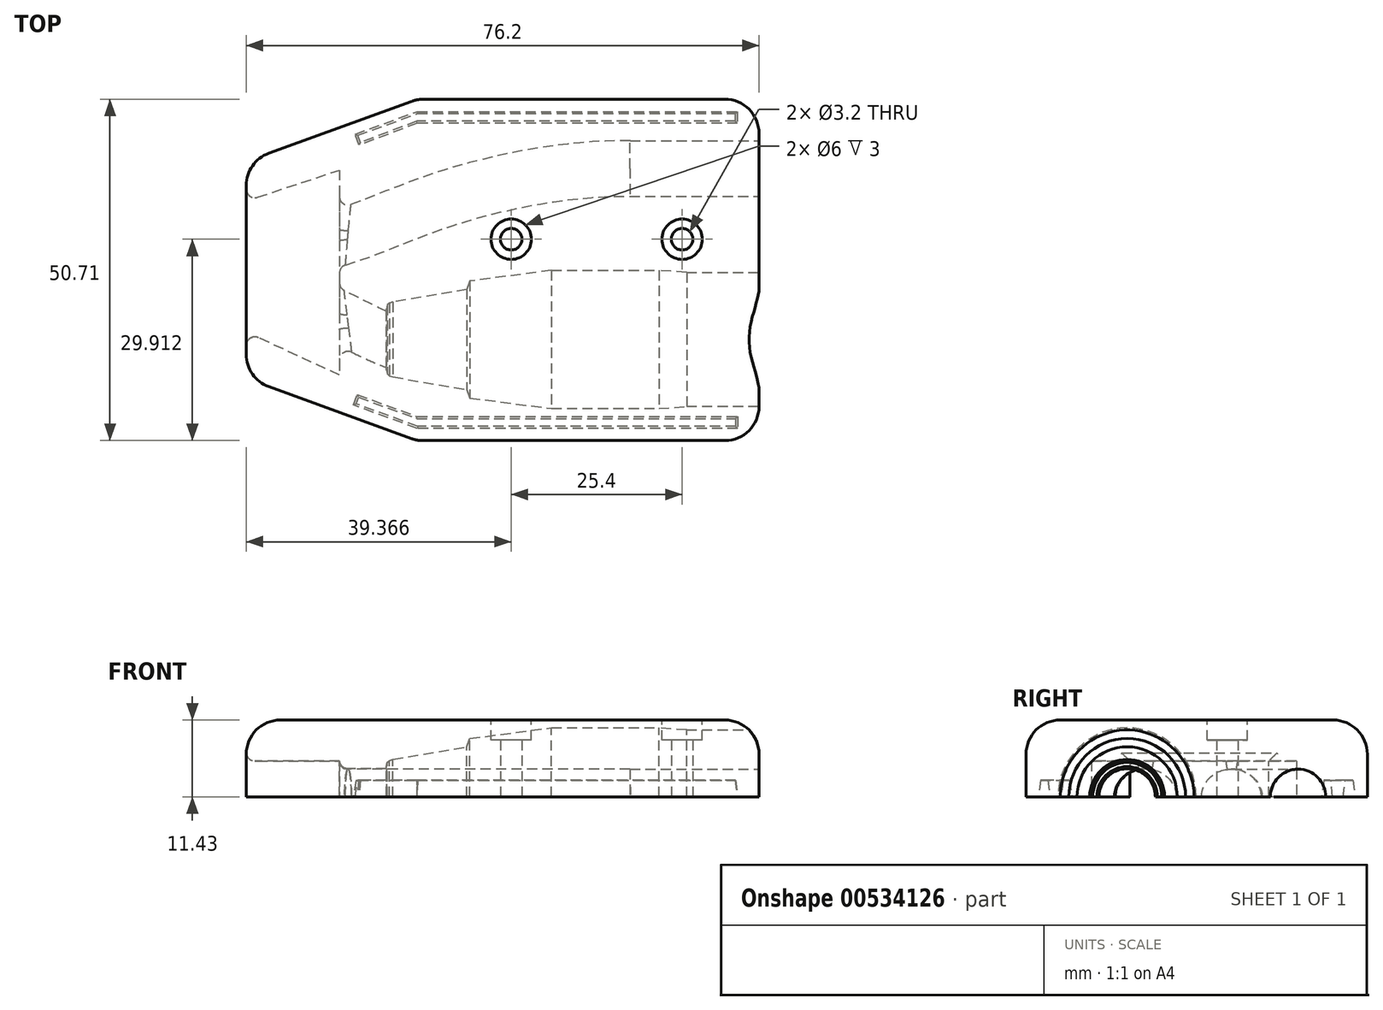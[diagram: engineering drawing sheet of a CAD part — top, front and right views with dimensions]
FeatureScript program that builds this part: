
annotation { "Feature Type Name" : "Feature", "Feature Type Description" : "" }
export const myFeature = defineFeature(function(context is Context, id is Id, definition is map)
    precondition{}
    {
        {
            var Q0;
            Q0=qCreatedBy(makeId("Top.planeOp"),FACE);
            var sketch = newSketch(context, id + "F0", { "sketchPlane" : qUnion([Q0])});
            skLineSegment(sketch, "E0", {"start": v(-28.61, 2.44) * mm, "end": v(45.8, 2.44) * mm});
            skLineSegment(sketch, "E1", {"start": v(45.8, 2.44) * mm, "end": v(45.8, -7.5) * mm});
            skLineSegment(sketch, "E2", {"start": v(45.8, -7.5) * mm, "end": v(33.92, -7.5) * mm});
            skLineSegment(sketch, "E3", {"start": v(33.92, -7.5) * mm, "end": v(31.07, -7.5) * mm});
            skLineSegment(sketch, "E4", {"start": v(31.07, -7.5) * mm, "end": v(15.98, -7.5) * mm});
            skLineSegment(sketch, "E5", {"start": v(15.98, -7.5) * mm, "end": v(11.85, -7.82) * mm});
            skLineSegment(sketch, "E6", {"start": v(11.85, -7.82) * mm, "end": v(-4.1, -7.82) * mm});
            skLineSegment(sketch, "E7", {"start": v(-4.1, -7.82) * mm, "end": v(-16.21, -6.24) * mm});
            skLineSegment(sketch, "E8", {"start": v(-16.21, -6.24) * mm, "end": v(-16.67, -5) * mm});
            skLineSegment(sketch, "E9", {"start": v(-16.67, -5) * mm, "end": v(-27.65, -3.12) * mm});
            skLineSegment(sketch, "E10", {"start": v(-27.65, -3.12) * mm, "end": v(-28.19, -2.96) * mm});
            skLineSegment(sketch, "E11", {"start": v(-28.19, -2.96) * mm, "end": v(-28.49, -2.68) * mm});
            skLineSegment(sketch, "E12", {"start": v(-28.49, -2.68) * mm, "end": v(-28.63, -2.06) * mm});
            skLineSegment(sketch, "E13", {"start": v(-28.63, -2.06) * mm, "end": v(-28.61, 2.44) * mm});
            skLineSegment(sketch, "E14.top", {"start": v(32.8, 22.64) * mm, "end": v(45.8, 22.64) * mm});
            skLineSegment(sketch, "E14.right", {"start": v(45.8, 27.84) * mm, "end": v(45.8, 22.64) * mm});
            skLineSegment(sketch, "E15", {"start": v(32.8, 23.72) * mm, "end": v(24.8, 23.72) * mm});
            skLineSegment(sketch, "E16", {"start": v(24.8, 23.72) * mm, "end": v(24.8, 27.84) * mm});
            skLineSegment(sketch, "E17", {"start": v(45.8, 27.84) * mm, "end": v(24.8, 27.84) * mm});
            skLineSegment(sketch, "E18", {"start": v(32.8, 22.64) * mm, "end": v(32.8, 23.72) * mm});
            skLineSegment(sketch, "E19.MirrorCS", {"start": v(32.8, 33.05) * mm, "end": v(32.8, 31.97) * mm});
            skLineSegment(sketch, "E20.MirrorCS", {"start": v(32.8, 33.05) * mm, "end": v(45.8, 33.05) * mm});
            skLineSegment(sketch, "E21.MirrorCS", {"start": v(45.8, 27.84) * mm, "end": v(45.8, 33.05) * mm});
            skLineSegment(sketch, "E22.MirrorCS", {"start": v(24.8, 31.97) * mm, "end": v(24.8, 27.84) * mm});
            skLineSegment(sketch, "E23.MirrorCS", {"start": v(32.8, 31.97) * mm, "end": v(24.8, 31.97) * mm});
            skLineSegment(sketch, "E24.MirrorCS", {"start": v(-28.19, 7.85) * mm, "end": v(-28.49, 7.56) * mm});
            skLineSegment(sketch, "E25.MirrorCS", {"start": v(-28.49, 7.56) * mm, "end": v(-28.63, 6.94) * mm});
            skLineSegment(sketch, "E26.MirrorCS", {"start": v(33.92, 12.39) * mm, "end": v(31.07, 12.39) * mm});
            skLineSegment(sketch, "E27.MirrorCS", {"start": v(-27.65, 8) * mm, "end": v(-28.19, 7.85) * mm});
            skLineSegment(sketch, "E28.MirrorCS", {"start": v(-16.21, 11.12) * mm, "end": v(-16.67, 9.89) * mm});
            skLineSegment(sketch, "E29.MirrorCS", {"start": v(-16.67, 9.89) * mm, "end": v(-27.65, 8) * mm});
            skLineSegment(sketch, "E30.MirrorCS", {"start": v(11.85, 12.7) * mm, "end": v(-4.1, 12.7) * mm});
            skLineSegment(sketch, "E31.MirrorCS", {"start": v(45.8, 12.39) * mm, "end": v(33.92, 12.39) * mm});
            skLineSegment(sketch, "E32.MirrorCS", {"start": v(-4.1, 12.7) * mm, "end": v(-16.21, 11.12) * mm});
            skLineSegment(sketch, "E33.MirrorCS", {"start": v(15.98, 12.39) * mm, "end": v(11.85, 12.7) * mm});
            skLineSegment(sketch, "E34.MirrorCS", {"start": v(31.07, 12.39) * mm, "end": v(15.98, 12.39) * mm});
            skLineSegment(sketch, "E35.MirrorCS", {"start": v(45.8, 2.44) * mm, "end": v(45.8, 12.39) * mm});
            skLineSegment(sketch, "E36.MirrorCS", {"start": v(-28.63, 6.94) * mm, "end": v(-28.61, 2.44) * mm});
            skSolve(sketch);
        }
        {
            var Q0;
            Q0=qCreatedBy(makeId("Top.planeOp"),FACE);
            var sketch = newSketch(context, id + "F1", { "sketchPlane" : qUnion([Q0])});
            skLineSegment(sketch, "E37.0", {"start": v(45.8, 2.44) * mm, "end": v(45.8, -7.5) * mm});
            skLineSegment(sketch, "E38.0", {"start": v(45.8, 27.84) * mm, "end": v(45.8, 22.64) * mm});
            skLineSegment(sketch, "E39", {"start": v(26.75, 38.13) * mm, "end": v(26.75, -12.58) * mm});
            skLineSegment(sketch, "E40", {"start": v(26.75, -12.58) * mm, "end": v(-24.05, -12.58) * mm});
            skLineSegment(sketch, "E41", {"start": v(-24.05, -12.58) * mm, "end": v(-49.45, -3.34) * mm});
            skLineSegment(sketch, "E42", {"start": v(-49.45, -3.34) * mm, "end": v(-49.45, 28.88) * mm});
            skLineSegment(sketch, "E43", {"start": v(-49.45, 28.88) * mm, "end": v(-24.05, 38.13) * mm});
            skLineSegment(sketch, "E44", {"start": v(-24.05, 38.13) * mm, "end": v(26.75, 38.13) * mm});
            skLineSegment(sketch, "E45.0", {"start": v(45.8, 27.84) * mm, "end": v(45.8, 33.05) * mm});
            skSolve(sketch);
        }
        {
            var Q0;
            Q0=qSketchRegion(id+"F1",true);
            extrude(context, id + "F2", {"entities" : qUnion([Q0]), "oppositeDirection" : true, "depth" : 0 * mm, "offsetDistance" : 25.4 * mm, "hasSecondDirection" : true, "secondDirectionOppositeDirection" : false, "secondDirectionDepth" : 11.43 * mm});
        }
        {
            var Q0;
            Q0=makeQuery(id+"F0.imprint","IMPRINT",FACE,{"disambiguationData":[TD([[makeQuery(id+"F0.imprint","IMPRINT",EDGE,{"derivedFrom":sQuery(id+"F0.wireOp",EDGE,"E0")}),-1.0]])]});
            var Q1;
            Q1=sQuery(id+"F0.wireOp",EDGE,"E0");
            revolve(context, id + "F3", {"operationType" : NewBodyOperationType.REMOVE, "entities" : qUnion([Q0]), "axis" : qUnion([Q1]), "revolveType" : RevolveType.FULL, "oppositeDirection" : true});
        }
        {
            var Q0;
            Q0=makeQuery(id+"F0.imprint","IMPRINT",FACE,{"disambiguationData":[TD([[makeQuery(id+"F0.imprint","IMPRINT",EDGE,{"derivedFrom":sQuery(id+"F0.wireOp",EDGE,"E14.top")}),1.0]])]});
            var Q1;
            Q1=sQuery(id+"F0.wireOp",EDGE,"E17");
            revolve(context, id + "F4", {"operationType" : NewBodyOperationType.REMOVE, "entities" : qUnion([Q0]), "axis" : qUnion([Q1]), "revolveType" : RevolveType.FULL});
        }
        {
            var Q0;
            Q0=qCreatedBy(makeId("Top.planeOp"),FACE);
            var sketch = newSketch(context, id + "F5", { "sketchPlane" : qUnion([Q0])});
            skLineSegment(sketch, "E46.0", {"start": v(-28.61, 2.44) * mm, "end": v(45.8, 2.44) * mm});
            skFitSpline(sketch, "E47", {"points": [v(-28.61, 2.44) * mm, v(-48.07, 10.49) * mm, v(-83.77, 9.93) * mm], "startDerivative": vector(-48.46, 20.5) * mm, "endDerivative": vector(-77.25, 2.74) * mm});
            skSolve(sketch);
        }
        {
            var Q0;
            Q0=sQuery(id+"F5.wireOp",VERTEX,"E47.0.internal");
            var Q1;
            Q1=sQuery(id+"F5.wireOp",EDGE,"E46.0");
            cPlane(context, id + "F6", {"entities" : qUnion([Q0, Q1]), "cplaneType" : CPlaneType.LINE_POINT, "offset" : 25.4 * mm, "width" : 152.4 * mm, "height" : 152.4 * mm});
        }
        {
            var Q0;
            Q0=qCreatedBy(id+"F6.planeOp",FACE);
            var sketch = newSketch(context, id + "F7", { "sketchPlane" : qUnion([Q0])});
            skCircle(sketch, "E48", {"center": v(2.44, 0) * mm, "radius": 4.2 * mm});
            skSolve(sketch);
        }
        {
            var Q0;
            Q0=qSketchRegion(id+"F7",true);
            var Q1;
            Q1=sQuery(id+"F5.wireOp",EDGE,"E47");
            sweep(context, id + "F8", {"operationType" : NewBodyOperationType.REMOVE, "profiles" : qUnion([Q0]), "path" : qUnion([Q1])});
        }
        {
            var Q0;
            Q0=sQuery(id+"F0.wireOp",VERTEX,"E22.MirrorCS.end");
            var Q1;
            Q1=sQuery(id+"F0.wireOp",EDGE,"E17");
            cPlane(context, id + "F9", {"entities" : qUnion([Q0, Q1]), "cplaneType" : CPlaneType.LINE_POINT, "offset" : 25.4 * mm, "width" : 152.4 * mm, "height" : 152.4 * mm});
        }
        {
            var Q0;
            Q0=qCreatedBy(makeId("Top.planeOp"),FACE);
            var sketch = newSketch(context, id + "F10", { "sketchPlane" : qUnion([Q0])});
            skLineSegment(sketch, "E49", {"start": v(24.8, 27.84) * mm, "end": v(7.57, 27.84) * mm});
            skFitSpline(sketch, "E50", {"points": [v(7.57, 27.84) * mm, v(-20.4, 23.18) * mm, v(-39.19, 16.58) * mm, v(-88.02, 16.43) * mm], "startDerivative": vector(-85.25, 1.29) * mm, "endDerivative": vector(-186.21, 7.59) * mm});
            skSolve(sketch);
        }
        {
            var Q0;
            Q0=qCreatedBy(id+"F9.planeOp",FACE);
            var sketch = newSketch(context, id + "F11", { "sketchPlane" : qUnion([Q0])});
            skCircle(sketch, "E51", {"center": v(-27.84, 0) * mm, "radius": 4.12 * mm});
            skSolve(sketch);
        }
        {
            var Q0;
            Q0=qSketchRegion(id+"F11",true);
            var Q1;
            Q1=sQuery(id+"F10.wireOp",EDGE,"E49");
            var Q2;
            Q2=sQuery(id+"F10.wireOp",EDGE,"E50");
            sweep(context, id + "F12", {"operationType" : NewBodyOperationType.REMOVE, "profiles" : qUnion([Q0]), "path" : qUnion([Q1, Q2])});
        }
        {
            var Q0;
            Q0=qCreatedBy(makeId("Top.planeOp"),FACE);
            var sketch = newSketch(context, id + "F13", { "sketchPlane" : qUnion([Q0])});
            skLineSegment(sketch, "E52", {"start": v(-49.97, 22.84) * mm, "end": v(-35.6, 27.6) * mm});
            skLineSegment(sketch, "E53", {"start": v(-35.6, 27.6) * mm, "end": v(-35.6, -2.85) * mm});
            skLineSegment(sketch, "E54", {"start": v(-35.6, -2.85) * mm, "end": v(-49.98, 3.8) * mm});
            skLineSegment(sketch, "E55", {"start": v(-49.97, 22.84) * mm, "end": v(-49.98, 3.8) * mm});
            skSolve(sketch);
        }
        {
            var Q0;
            Q0=qCreatedBy(makeId("Top.planeOp"),FACE);
            var sketch = newSketch(context, id + "F14", { "sketchPlane" : qUnion([Q0])});
            skCircle(sketch, "E56", {"center": v(-10.08, 17.33) * mm, "radius": 1.6 * mm});
            skCircle(sketch, "E57", {"center": v(15.32, 17.33) * mm, "radius": 1.6 * mm});
            skLineSegment(sketch, "E58.0", {"start": v(-24.05, 38.13) * mm, "end": v(26.75, 38.13) * mm});
            skLineSegment(sketch, "E59.0", {"start": v(26.75, -12.58) * mm, "end": v(-24.05, -12.58) * mm});
            skLineSegment(sketch, "E60.0", {"start": v(-49.45, 28.88) * mm, "end": v(-24.05, 38.13) * mm});
            skLineSegment(sketch, "E61.0", {"start": v(-24.05, -12.58) * mm, "end": v(-49.45, -3.34) * mm});
            skSolve(sketch);
        }
        {
            var Q0;
            Q0=qCreatedBy(makeId("Top.planeOp"),FACE);
            var sketch = newSketch(context, id + "F15", { "sketchPlane" : qUnion([Q0])});
            skLineSegment(sketch, "E62.0", {"start": v(-49.45, 28.88) * mm, "end": v(-24.05, 38.13) * mm});
            skLineSegment(sketch, "E63.0", {"start": v(-24.05, 38.13) * mm, "end": v(26.75, 38.13) * mm});
            skLineSegment(sketch, "E64.0", {"start": v(-24.05, -12.58) * mm, "end": v(-49.45, -3.34) * mm});
            skLineSegment(sketch, "E65.1", {"start": v(26.75, -12.58) * mm, "end": v(-24.05, -12.58) * mm});
            skLineSegment(sketch, "E66", {"start": v(-33.28, 32.94) * mm, "end": v(-24.05, 36.3) * mm});
            skLineSegment(sketch, "E67", {"start": v(-24.05, 36.3) * mm, "end": v(23.52, 36.3) * mm});
            skLineSegment(sketch, "E68", {"start": v(23.52, 36.3) * mm, "end": v(23.52, 34.55) * mm});
            skLineSegment(sketch, "E69", {"start": v(23.52, 34.55) * mm, "end": v(-24.05, 34.55) * mm});
            skLineSegment(sketch, "E70", {"start": v(-33.28, 32.94) * mm, "end": v(-32.69, 31.3) * mm});
            skLineSegment(sketch, "E71", {"start": v(-32.69, 31.3) * mm, "end": v(-24.05, 34.55) * mm});
            skLineSegment(sketch, "E72", {"start": v(-33.53, -7.3) * mm, "end": v(-24.05, -10.76) * mm});
            skLineSegment(sketch, "E73", {"start": v(-24.05, -10.76) * mm, "end": v(23.57, -10.76) * mm});
            skLineSegment(sketch, "E74", {"start": v(23.57, -10.76) * mm, "end": v(23.57, -9) * mm});
            skLineSegment(sketch, "E75", {"start": v(23.57, -9) * mm, "end": v(-24.05, -9) * mm});
            skLineSegment(sketch, "E76", {"start": v(-24.05, -9) * mm, "end": v(-32.97, -5.76) * mm});
            skLineSegment(sketch, "E77", {"start": v(-32.97, -5.76) * mm, "end": v(-33.53, -7.3) * mm});
            skSolve(sketch);
        }
        {
            var Q0;
            Q0 = qSketchRegion(id + "F13", true);
            extrude(context, id + "F16", {"entities" : qUnion([Q0]), "operationType" : NewBodyOperationType.REMOVE, "depth" : 5.33 * mm, "offsetDistance" : 25.4 * mm});
        }
        {
            var Q0;
            Q0 = qSketchRegion(id + "F15", true);
            extrude(context, id + "F17", {"entities" : qUnion([Q0]), "operationType" : NewBodyOperationType.REMOVE, "depth" : 2.5 * mm, "offsetDistance" : 25.4 * mm, "hasDraft" : true, "draftAngle" : 7 * degree, "draftPullDirection" : true});
        }
        {
            var Q0;
            Q0 = qSketchRegion(id + "F14", true);
            extrude(context, id + "F18", {"entities" : qUnion([Q0]), "operationType" : NewBodyOperationType.REMOVE, "depth" : 25.4 * mm, "offsetDistance" : 25.4 * mm});
        }
        {
            var Q0;
            Q0=makeQuery(id+"F2.opExtrude","CAP_FACE",FACE,{"disambiguationData":[OSD([sQuery(id+"F1.wireOp",EDGE,"E39"),sQuery(id+"F1.wireOp",EDGE,"E40"),sQuery(id+"F1.wireOp",EDGE,"E41"),sQuery(id+"F1.wireOp",EDGE,"E42"),sQuery(id+"F1.wireOp",EDGE,"E43"),sQuery(id+"F1.wireOp",EDGE,"E44")])],"isStart":true});
            var sketch = newSketch(context, id + "F19", { "sketchPlane" : qUnion([Q0])});
            skCircle(sketch, "E78.0", {"center": v(-10.08, 17.33) * mm, "radius": 1.6 * mm});
            skCircle(sketch, "E79.0", {"center": v(15.32, 17.33) * mm, "radius": 1.6 * mm});
            skCircle(sketch, "E80", {"center": v(-10.08, 17.33) * mm, "radius": 3 * mm});
            skCircle(sketch, "E81", {"center": v(15.32, 17.33) * mm, "radius": 3 * mm});
            skSolve(sketch);
        }
        {
            var Q0;
            Q0 = qSketchRegion(id + "F19", true);
            extrude(context, id + "F20", {"entities" : qUnion([Q0]), "operationType" : NewBodyOperationType.REMOVE, "oppositeDirection" : true, "depth" : 3 * mm, "offsetDistance" : 25.4 * mm});
        }
        {
            var Q0;
            Q0=makeQuery(id+"F16.boolean.opBoolean","INTERSECT",EDGE,{"derivedFrom":[makeQuery(id+"F2.opExtrude","SWEPT_FACE",FACE,{"disambiguationData":[OSD([sQuery(id+"F1.wireOp",EDGE,"E42")])]}),makeQuery(id+"F16.opExtrude","CAP_FACE",FACE,{"disambiguationData":[OSD([sQuery(id+"F13.wireOp",EDGE,"E52"),sQuery(id+"F13.wireOp",EDGE,"E53"),sQuery(id+"F13.wireOp",EDGE,"E54"),sQuery(id+"F13.wireOp",EDGE,"E55")])],"isStart":false})]});
            var Q1;
            Q1=makeQuery(id+"F16.boolean.opBoolean","INTERSECT",EDGE,{"derivedFrom":[makeQuery(id+"F2.opExtrude","SWEPT_FACE",FACE,{"disambiguationData":[OSD([sQuery(id+"F1.wireOp",EDGE,"E42")])]}),makeQuery(id+"F16.opExtrude","SWEPT_FACE",FACE,{"disambiguationData":[OSD([sQuery(id+"F13.wireOp",EDGE,"E54")])]})]});
            var Q2;
            Q2=makeQuery(id+"F16.boolean.opBoolean","INTERSECT",EDGE,{"derivedFrom":[makeQuery(id+"F2.opExtrude","SWEPT_FACE",FACE,{"disambiguationData":[OSD([sQuery(id+"F1.wireOp",EDGE,"E42")])]}),makeQuery(id+"F16.opExtrude","SWEPT_FACE",FACE,{"disambiguationData":[OSD([sQuery(id+"F13.wireOp",EDGE,"E52")])]})]});
            fillet(context, id + "F21", {"entities" : qUnion([Q0, Q1, Q2]), "radius" : 1.27 * mm, "tangentPropagation" : true, "allowEdgeOverflow" : false});
        }
        {
            var Q0;
            Q0=makeQuery(id+"F16.boolean.opBoolean","INTERSECT",EDGE,{"derivedFrom":[makeQuery(id+"F8.boolean.opBoolean","COPY",FACE,{"derivedFrom":makeQuery(id+"F8.opSweep","SWEPT_FACE",FACE,{"disambiguationData":[OSD([sQuery(id+"F5.wireOp",EDGE,"E47"),sQuery(id+"F7.wireOp",EDGE,"E48")])]})}),makeQuery(id+"F16.opExtrude","SWEPT_FACE",FACE,{"disambiguationData":[OSD([sQuery(id+"F13.wireOp",EDGE,"E53")])]})]});
            var Q1;
            Q1=makeQuery(id+"F16.boolean.opBoolean","INTERSECT",EDGE,{"derivedFrom":[makeQuery(id+"F12.boolean.opBoolean","COPY",FACE,{"derivedFrom":makeQuery(id+"F12.opSweep","SWEPT_FACE",FACE,{"disambiguationData":[OSD([sQuery(id+"F10.wireOp",EDGE,"E50"),sQuery(id+"F11.wireOp",EDGE,"E51")])]})}),makeQuery(id+"F16.opExtrude","SWEPT_FACE",FACE,{"disambiguationData":[OSD([sQuery(id+"F13.wireOp",EDGE,"E53")])]})]});
            fillet(context, id + "F22", {"entities" : qUnion([Q0, Q1]), "radius" : 1.27 * mm, "tangentPropagation" : true, "allowEdgeOverflow" : false});
        }
        {
            var Q0;
            Q0=makeQuery(id+"F2.opExtrude","SWEPT_EDGE",EDGE,{"disambiguationData":[OSD([sQuery(id+"F1.wireOp",EDGE,"E42"),sQuery(id+"F1.wireOp",EDGE,"E43")])]});
            var Q1;
            Q1=makeQuery(id+"F2.opExtrude","CAP_EDGE",EDGE,{"disambiguationData":[OSD([sQuery(id+"F1.wireOp",EDGE,"E42")])],"isStart":true});
            var Q2;
            Q2=makeQuery(id+"F2.opExtrude","CAP_EDGE",EDGE,{"disambiguationData":[OSD([sQuery(id+"F1.wireOp",EDGE,"E43")])],"isStart":true});
            var Q3;
            Q3=makeQuery(id+"F2.opExtrude","SWEPT_EDGE",EDGE,{"disambiguationData":[OSD([sQuery(id+"F1.wireOp",EDGE,"E43"),sQuery(id+"F1.wireOp",EDGE,"E44")])]});
            var Q4;
            Q4=makeQuery(id+"F2.opExtrude","CAP_EDGE",EDGE,{"disambiguationData":[OSD([sQuery(id+"F1.wireOp",EDGE,"E44")])],"isStart":true});
            var Q5;
            Q5=makeQuery(id+"F2.opExtrude","SWEPT_EDGE",EDGE,{"disambiguationData":[OSD([sQuery(id+"F1.wireOp",EDGE,"E39"),sQuery(id+"F1.wireOp",EDGE,"E44")])]});
            var Q6;
            Q6=makeQuery(id+"F2.opExtrude","CAP_EDGE",EDGE,{"disambiguationData":[OSD([sQuery(id+"F1.wireOp",EDGE,"E39")])],"isStart":true});
            var Q7;
            Q7=makeQuery(id+"F2.opExtrude","SWEPT_EDGE",EDGE,{"disambiguationData":[OSD([sQuery(id+"F1.wireOp",EDGE,"E39"),sQuery(id+"F1.wireOp",EDGE,"E40")])]});
            var Q8;
            Q8=makeQuery(id+"F2.opExtrude","CAP_EDGE",EDGE,{"disambiguationData":[OSD([sQuery(id+"F1.wireOp",EDGE,"E40")])],"isStart":true});
            var Q9;
            Q9=makeQuery(id+"F2.opExtrude","SWEPT_EDGE",EDGE,{"disambiguationData":[OSD([sQuery(id+"F1.wireOp",EDGE,"E40"),sQuery(id+"F1.wireOp",EDGE,"E41")])]});
            var Q10;
            Q10=makeQuery(id+"F2.opExtrude","CAP_EDGE",EDGE,{"disambiguationData":[OSD([sQuery(id+"F1.wireOp",EDGE,"E41")])],"isStart":true});
            var Q11;
            Q11=makeQuery(id+"F2.opExtrude","SWEPT_EDGE",EDGE,{"disambiguationData":[OSD([sQuery(id+"F1.wireOp",EDGE,"E41"),sQuery(id+"F1.wireOp",EDGE,"E42")])]});
            fillet(context, id + "F23", {"entities" : qUnion([Q0, Q1, Q2, Q3, Q4, Q5, Q6, Q7, Q8, Q9, Q10, Q11]), "radius" : 5.08 * mm, "tangentPropagation" : true, "allowEdgeOverflow" : false});
        }
    });
